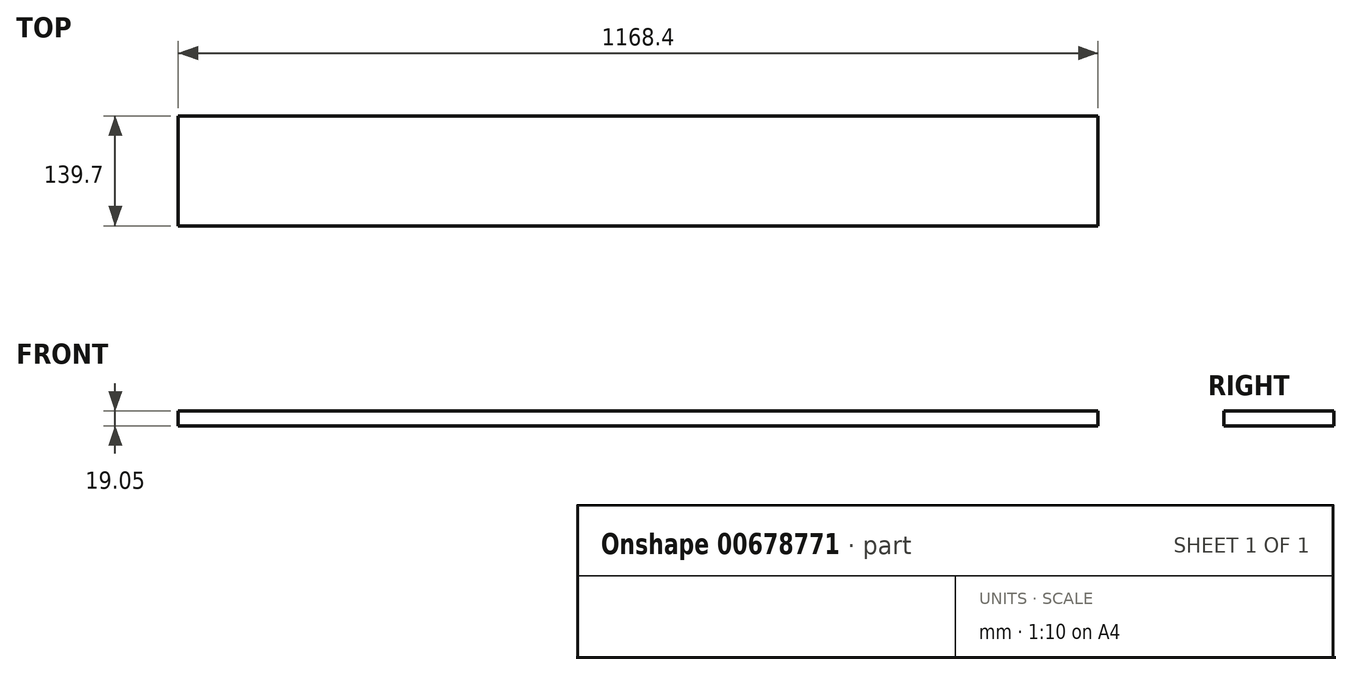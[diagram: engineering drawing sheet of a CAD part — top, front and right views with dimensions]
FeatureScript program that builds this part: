
annotation { "Feature Type Name" : "Feature", "Feature Type Description" : "" }
export const myFeature = defineFeature(function(context is Context, id is Id, definition is map)
    precondition{}
    {
        {
            var Q0;
            Q0=qCreatedBy(makeId("Top.planeOp"),FACE);
            var sketch = newSketch(context, id + "F0", { "sketchPlane" : qUnion([Q0])});
            skLineSegment(sketch, "E0.bottom", {"start": v(-711.8, 101.45) * mm, "end": v(456.6, 101.45) * mm});
            skLineSegment(sketch, "E0.top", {"start": v(-711.8, -38.25) * mm, "end": v(456.6, -38.25) * mm});
            skLineSegment(sketch, "E0.left", {"start": v(-711.8, 101.45) * mm, "end": v(-711.8, -38.25) * mm});
            skLineSegment(sketch, "E0.right", {"start": v(456.6, 101.45) * mm, "end": v(456.6, -38.25) * mm});
            skSolve(sketch);
        }
        {
            var Q0;
            Q0=makeQuery(id+"F0.imprint","IMPRINT",FACE,{"disambiguationData":[TD([[makeQuery(id+"F0.imprint","IMPRINT",EDGE,{"derivedFrom":sQuery(id+"F0.wireOp",EDGE,"E0.bottom")}),-1.0]])]});
            extrude(context, id + "F1", {"entities" : qUnion([Q0]), "depth" : 19.05 * mm, "offsetDistance" : 25.4 * mm});
        }
    });
